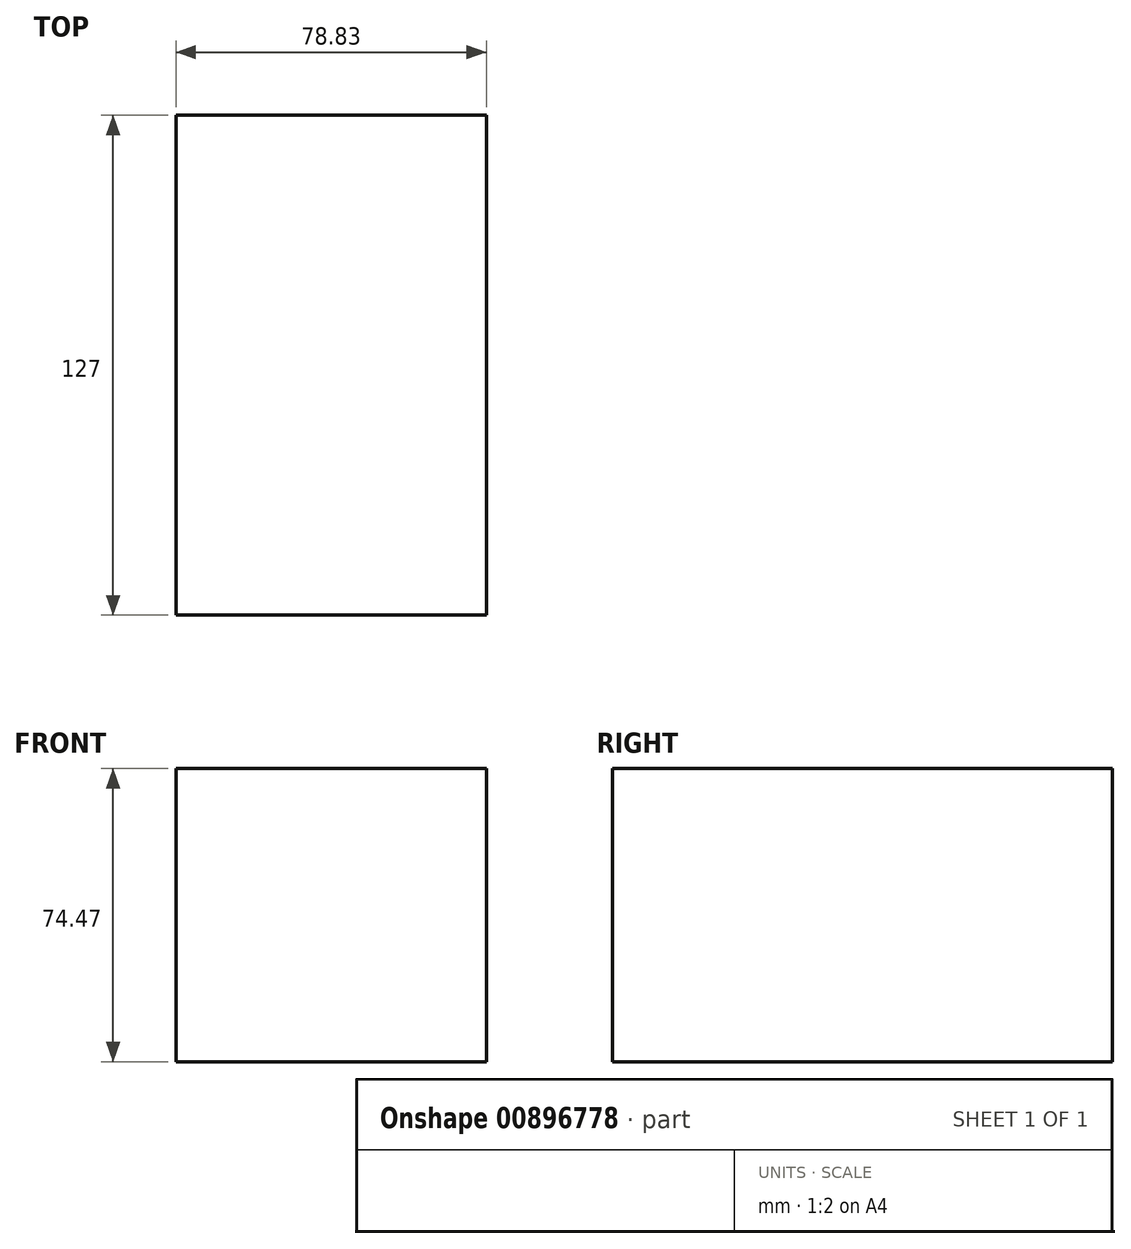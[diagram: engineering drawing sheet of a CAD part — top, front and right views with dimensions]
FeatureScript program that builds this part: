
annotation { "Feature Type Name" : "Feature", "Feature Type Description" : "" }
export const myFeature = defineFeature(function(context is Context, id is Id, definition is map)
    precondition{}
    {
        {
            var Q0;
            Q0=qCreatedBy(makeId("Front.planeOp"),FACE);
            var sketch = newSketch(context, id + "F0", { "sketchPlane" : qUnion([Q0])});
            skLineSegment(sketch, "E0.bottom", {"start": v(-41, 31.89) * mm, "end": v(37.83, 31.89) * mm});
            skLineSegment(sketch, "E0.top", {"start": v(-41, -42.58) * mm, "end": v(37.83, -42.58) * mm});
            skLineSegment(sketch, "E0.left", {"start": v(-41, 31.89) * mm, "end": v(-41, -42.58) * mm});
            skLineSegment(sketch, "E0.right", {"start": v(37.83, 31.89) * mm, "end": v(37.83, -42.58) * mm});
            skSolve(sketch);
        }
        {
            var Q0;
            Q0=makeQuery(id+"F0.imprint","IMPRINT",FACE,{"disambiguationData":[TD([[makeQuery(id+"F0.imprint","IMPRINT",EDGE,{"derivedFrom":sQuery(id+"F0.wireOp",EDGE,"E0.bottom")}),-1.0]])]});
            extrude(context, id + "F1", {"entities" : qUnion([Q0]), "depth" : 127 * mm, "offsetDistance" : 25.4 * mm});
        }
    });
